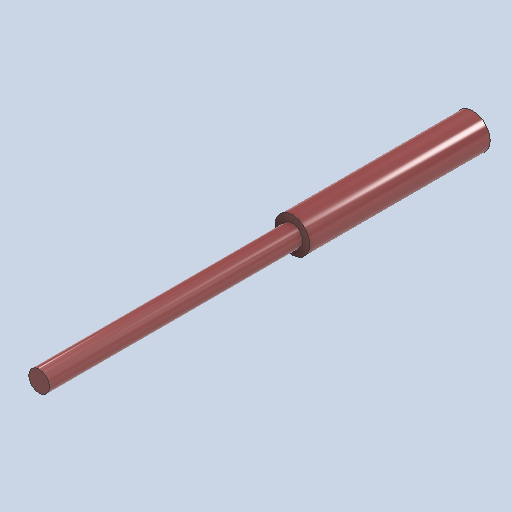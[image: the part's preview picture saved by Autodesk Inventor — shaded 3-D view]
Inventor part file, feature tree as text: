
AUTODESK INVENTOR PART (.ipt)
format: ipt  version: 2025.2 (Build 292293000, 293)  size: 106,496 bytes
history: native  units: mm
features: extrude x2, sketch x1
ambient origin geometry x8: Origin, YZ Plane, XZ Plane, XY Plane, X Axis, Y Axis, Z Axis, Center Point
bodies: Solid1 (feature_tree)
feature tree (3):
  sketch  "Sketch1"  dims[d0=5.0mm d1=3.0mm d2=36.5mm d3=0.0mm d4=26.0mm d5=0.0mm]
  extrude  "Extrusion1"  Depth=26.0mm
  extrude  "Extrusion2"  Depth=36.5mm TaperAngle=0.0deg
